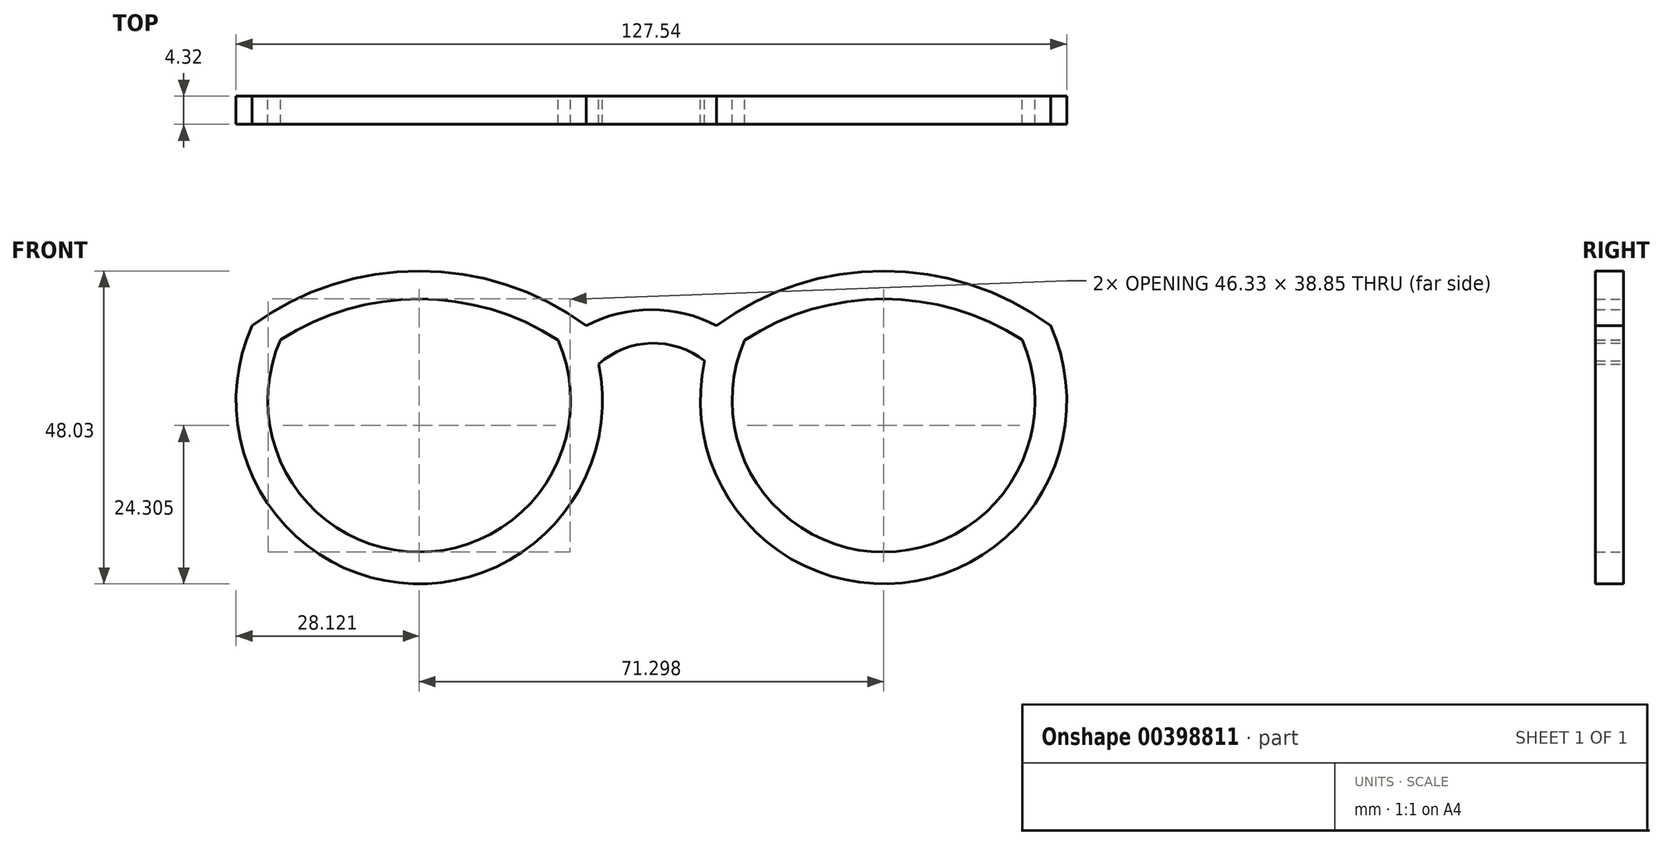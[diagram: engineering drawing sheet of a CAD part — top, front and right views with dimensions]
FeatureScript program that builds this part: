
annotation { "Feature Type Name" : "Feature", "Feature Type Description" : "" }
export const myFeature = defineFeature(function(context is Context, id is Id, definition is map)
    precondition{}
    {
        {
            var Q0;
            Q0=qCreatedBy(makeId("Front.planeOp"),FACE);
            var sketch = newSketch(context, id + "F0", { "sketchPlane" : qUnion([Q0])});
            skArc(sketch, "E0", {"start": v(9.99, 0) * mm, "mid": v(35.65, -39.64) * mm, "end": v(61.3, 0) * mm});
            skArc(sketch, "E1", {"start": v(61.3, 0) * mm, "mid": v(35.65, 8.4) * mm, "end": v(9.99, 0) * mm});
            skArc(sketch, "E2", {"start": v(14.34, -2.22) * mm, "mid": v(35.67, -34.76) * mm, "end": v(56.94, -2.18) * mm});
            skArc(sketch, "E3", {"start": v(56.94, -2.18) * mm, "mid": v(35.63, 4.1) * mm, "end": v(14.34, -2.22) * mm});
            skArc(sketch, "E4.MirrorCS", {"start": v(-61.3, 0) * mm, "mid": v(-35.65, 8.4) * mm, "end": v(-9.99, 0) * mm});
            skArc(sketch, "E5.MirrorCS", {"start": v(-56.94, -2.18) * mm, "mid": v(-35.63, 4.1) * mm, "end": v(-14.34, -2.22) * mm});
            skArc(sketch, "E6.MirrorCS", {"start": v(-9.99, 0) * mm, "mid": v(-35.65, -39.64) * mm, "end": v(-61.3, 0) * mm});
            skArc(sketch, "E7.MirrorCS", {"start": v(-14.34, -2.22) * mm, "mid": v(-35.67, -34.76) * mm, "end": v(-56.94, -2.18) * mm});
            skArc(sketch, "E8", {"start": v(9.99, 0) * mm, "mid": v(0, 2.45) * mm, "end": v(-9.99, 0) * mm});
            skArc(sketch, "E9", {"start": v(8.2, -5.42) * mm, "mid": v(-0.04, -2.7) * mm, "end": v(-8.1, -5.9) * mm});
            skSolve(sketch);
        }
        {
            var Q0;
            Q0=qSketchRegion(id+"F0",true);
            extrude(context, id + "F1", {"entities" : qUnion([Q0]), "depth" : 4.32 * mm});
        }
    });
